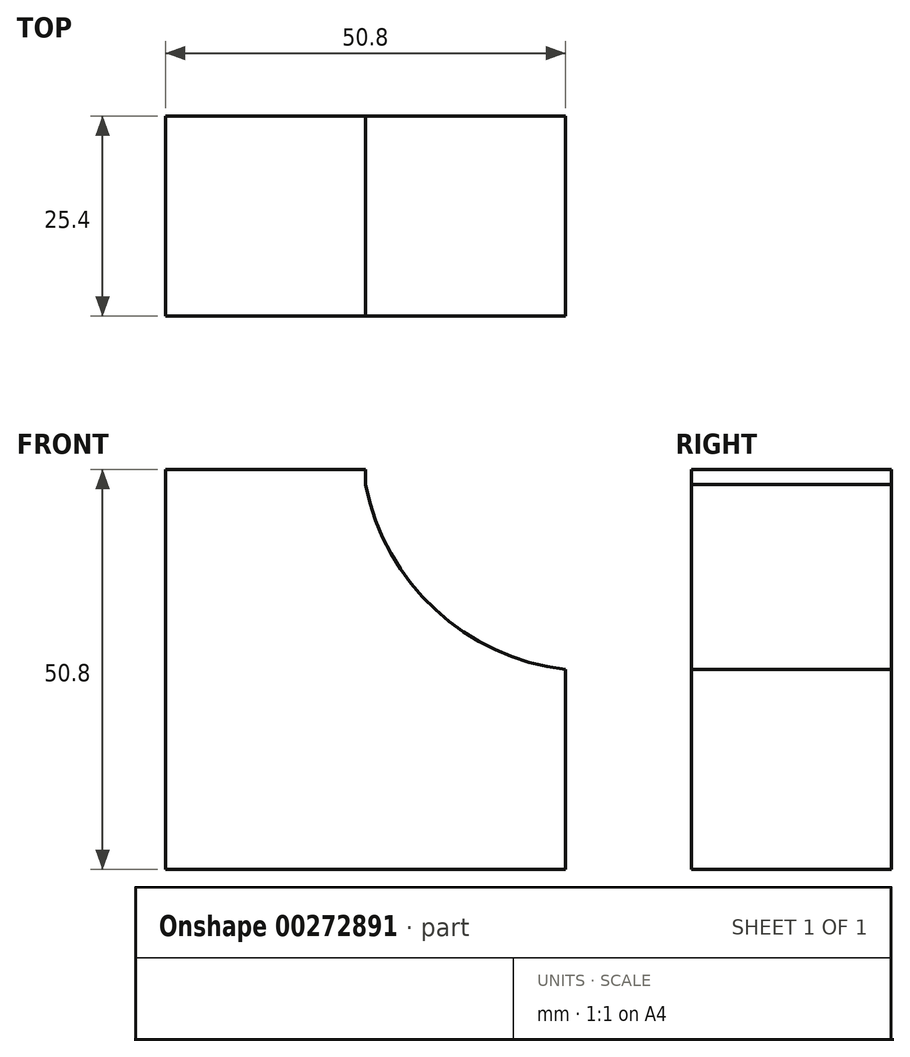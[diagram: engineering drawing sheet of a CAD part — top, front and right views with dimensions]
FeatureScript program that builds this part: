
annotation { "Feature Type Name" : "Feature", "Feature Type Description" : "" }
export const myFeature = defineFeature(function(context is Context, id is Id, definition is map)
    precondition{}
    {
        {
            var Q0;
            Q0=qCreatedBy(makeId("Front.planeOp"),FACE);
            var sketch = newSketch(context, id + "F0", { "sketchPlane" : qUnion([Q0])});
            skLineSegment(sketch, "E0", {"start": v(0, 0) * mm, "end": v(-50.8, 0) * mm});
            skLineSegment(sketch, "E1", {"start": v(-50.8, 0) * mm, "end": v(-50.8, 50.8) * mm});
            skLineSegment(sketch, "E2", {"start": v(-25.4, 50.8) * mm, "end": v(-50.8, 50.8) * mm});
            skPoint(sketch, "E3.start.orphan", {"position": v(-25.4, 48.88) * mm});
            skLineSegment(sketch, "E4", {"start": v(-25.4, 50.8) * mm, "end": v(-25.4, 48.88) * mm});
            skLineSegment(sketch, "E5", {"start": v(0, 25.4) * mm, "end": v(0, 0) * mm});
            skPoint(sketch, "E6.start.orphan", {"position": v(-25.4, 25.4) * mm});
            skArc(sketch, "E7", {"start": v(-25.4, 48.88) * mm, "mid": v(-16.53, 33) * mm, "end": v(0, 25.4) * mm});
            skSolve(sketch);
        }
        {
            var Q0;
            Q0=makeQuery(id+"F0.imprint","IMPRINT",FACE,{"disambiguationData":[TD([[makeQuery(id+"F0.imprint","IMPRINT",EDGE,{"derivedFrom":sQuery(id+"F0.wireOp",EDGE,"E0")}),-1.0]])]});
            extrude(context, id + "F1", {"entities" : qUnion([Q0]), "depth" : 25.4 * mm});
        }
    });
